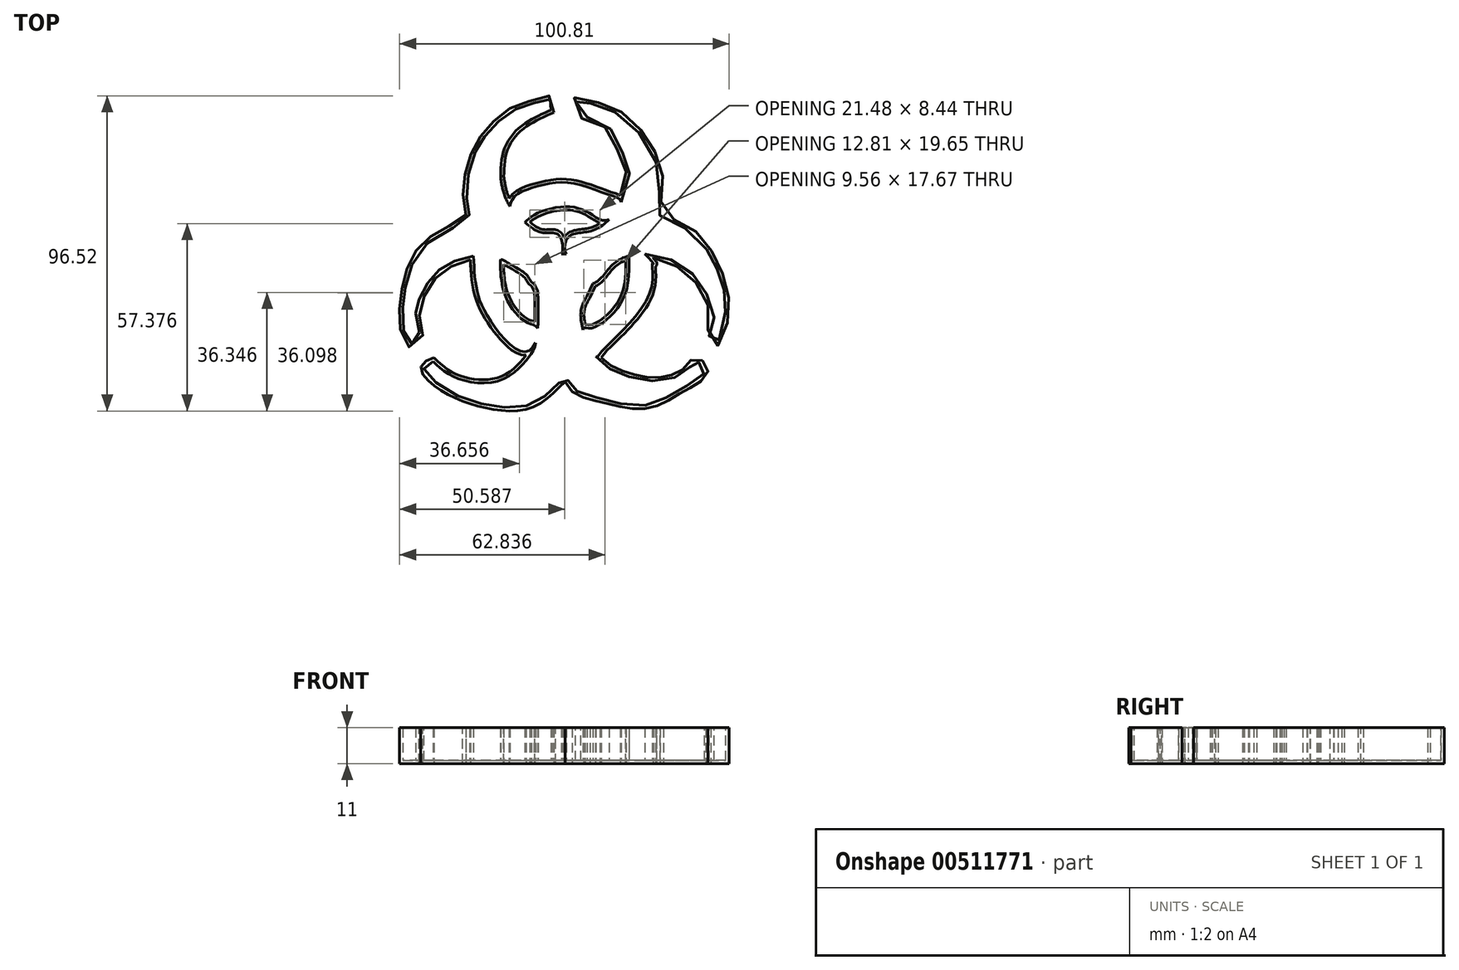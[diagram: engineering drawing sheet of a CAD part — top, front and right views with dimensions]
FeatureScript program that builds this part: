
annotation { "Feature Type Name" : "Feature", "Feature Type Description" : "" }
export const myFeature = defineFeature(function(context is Context, id is Id, definition is map)
    precondition{}
    {
        {
            var Q0;
            Q0=qCreatedBy(makeId("Top.planeOp"),FACE);
            var sketch = newSketch(context, id + "F0", { "sketchPlane" : qUnion([Q0])});
            skFitSpline(sketch, "E0", {"points": [v(-7.67, 51.18) * mm, v(-12.75, 48.8) * mm, v(-18.4, 44.85) * mm, v(-22.23, 38.53) * mm, v(-23.14, 30.74) * mm], "startDerivative": vector(-22.22, -9.67) * mm, "endDerivative": vector(-0.85, -30.02) * mm});
            skFitSpline(sketch, "E1", {"points": [v(-23.14, 30.74) * mm, v(-21.9, 24.98) * mm, v(-18.62, 19.45) * mm, v(-14.33, 15.72) * mm, v(-10.04, 13.57) * mm, v(-5.3, 12.9) * mm, v(-4.5, 7.14) * mm, v(-6.23, 6.65) * mm, v(-8.7, 3.81) * mm, v(-8.56, 0.6) * mm, v(-12.94, -1.87) * mm, v(-14.76, 0.22) * mm, v(-18.58, 3.02) * mm, v(-23.14, 5.54) * mm, v(-26.6, 6.37) * mm, v(-31.42, 6.5) * mm, v(-39.15, 4.06) * mm, v(-44.05, 0.16) * mm, v(-48.07, -6.62) * mm, v(-49.07, -10.95) * mm, v(-48.13, -18.6) * mm, v(-51.11, -20.32) * mm, v(-53.05, -11.45) * mm, v(-52.02, -1.94) * mm, v(-45.68, 10.35) * mm, v(-32.93, 18.54) * mm, v(-33.61, 24.7) * mm, v(-31.21, 37.43) * mm, v(-27.68, 43.51) * mm, v(-20.34, 50.45) * mm, v(-12.75, 53.38) * mm, v(-7.67, 54.36) * mm, v(-7.67, 51.18) * mm], "startDerivative": vector(27.16, -188.43) * mm, "endDerivative": vector(-39.63, -181.1) * mm});
            skFitSpline(sketch, "E2", {"points": [v(-20.34, 21.78) * mm, v(-18.62, 24.98) * mm, v(-11.51, 27.94) * mm, v(-1.52, 28.86) * mm, v(10.79, 24.98) * mm, v(13.71, 23.02) * mm, v(9.56, 17.48) * mm, v(4.33, 19.45) * mm, v(-2.75, 21.63) * mm, v(-12.13, 19.45) * mm, v(-15.77, 16.82) * mm], "startDerivative": vector(14.78, 47.04) * mm, "endDerivative": vector(-37.06, -33.58) * mm});
            skFitSpline(sketch, "E3", {"points": [v(0.64, 50.45) * mm, v(8.64, 47.32) * mm, v(13.71, 38.86) * mm, v(16.17, 33.4) * mm, v(13.71, 23.02) * mm, v(5.25, 14.4) * mm, v(-2.44, 12.25) * mm, v(-3.05, 7.17) * mm, v(-0.77, 6) * mm, v(1.57, 2.33) * mm, v(0.96, 0.2) * mm, v(5.13, -1.84) * mm, v(11.34, 4.06) * mm, v(21, 7.14) * mm, v(30.07, 4.87) * mm, v(36.99, -0.42) * mm, v(40.96, -7.54) * mm, v(41.97, -14.46) * mm, v(40.65, -18.53) * mm, v(42.69, -20.16) * mm, v(45.47, -12.22) * mm, v(45.47, -5.3) * mm, v(43.6, 1.31) * mm, v(41.36, 6.2) * mm, v(34.04, 14.64) * mm, v(25.18, 19.45) * mm, v(25.62, 27.91) * mm, v(21.83, 40.46) * mm, v(12.1, 50.45) * mm, v(4.03, 53.38) * mm, v(0.23, 54.36) * mm, v(0.64, 50.45) * mm]});
            skFitSpline(sketch, "E4", {"points": [v(21, 7.14) * mm, v(23.7, 4.14) * mm, v(23.39, 4.3) * mm, v(22.6, -4.59) * mm, v(7.62, -23) * mm, v(5.98, -24.22) * mm, v(2.1, -15.64) * mm, v(3.94, -15.64) * mm, v(13.71, -7.88) * mm, v(16.17, 6.57) * mm], "startDerivative": vector(49.86, -54.06) * mm, "endDerivative": vector(-1.43, 92.76) * mm});
            skFitSpline(sketch, "E5", {"points": [v(5.13, -1.84) * mm, v(3.4, -5.68) * mm], "startDerivative": vector(-1.74, -3.84) * mm, "endDerivative": vector(-1.74, -3.84) * mm});
            skFitSpline(sketch, "E6", {"points": [v(0.96, 0.2) * mm, v(-0.95, -1.84) * mm], "startDerivative": vector(-1.92, -2.04) * mm, "endDerivative": vector(-1.92, -2.04) * mm});
            skFitSpline(sketch, "E7", {"points": [v(-8.56, 0.6) * mm, v(-6.68, -1.84) * mm], "startDerivative": vector(1.88, -2.44) * mm, "endDerivative": vector(1.88, -2.44) * mm});
            skFitSpline(sketch, "E8", {"points": [v(-12.94, -1.87) * mm, v(-11.23, -5.29) * mm], "startDerivative": vector(1.71, -3.41) * mm, "endDerivative": vector(1.71, -3.41) * mm});
            skFitSpline(sketch, "E9", {"points": [v(-5.3, 12.9) * mm, v(-2.44, 12.25) * mm], "startDerivative": vector(2.86, -0.65) * mm, "endDerivative": vector(2.86, -0.65) * mm});
            skFitSpline(sketch, "E10", {"points": [v(-4.5, 7.14) * mm, v(-3.05, 7.17) * mm], "startDerivative": vector(1.45, 0.04) * mm, "endDerivative": vector(1.45, 0.04) * mm});
            skFitSpline(sketch, "E11", {"points": [v(-23.14, 5.54) * mm, v(-23.14, 1.94) * mm, v(-21.35, -6.55) * mm, v(-15.1, -13.79) * mm, v(-11.61, -16.04) * mm, v(-15.1, -22.78) * mm, v(-26.6, -12.8) * mm, v(-30.58, -3.06) * mm, v(-31.42, 6.5) * mm], "startDerivative": vector(-1.25, -38.8) * mm, "endDerivative": vector(-3.41, 73.3) * mm});
            skFitSpline(sketch, "E12", {"points": [v(-43.81, -25.77) * mm, v(-36.82, -30.76) * mm, v(-23.14, -31.51) * mm, v(-14.76, -24.77) * mm, v(-12.37, -20.1) * mm, v(-11.61, -9.8) * mm, v(-11.8, -4.15) * mm], "startDerivative": vector(35.95, -33.84) * mm, "endDerivative": vector(-2, 37.23) * mm});
            skFitSpline(sketch, "E13", {"points": [v(-43.81, -25.77) * mm, v(-46.56, -27.77) * mm, v(-40.07, -34.26) * mm, v(-26.6, -39.23) * mm, v(-14.76, -39.23) * mm, v(-6.68, -33.76) * mm, v(-3.12, -31.01) * mm, v(-1.13, -33.76) * mm, v(6.86, -37) * mm, v(21.09, -39.23) * mm, v(32.07, -34.26) * mm, v(39.31, -28.52) * mm, v(36.57, -25.77) * mm, v(34.07, -28.27) * mm, v(24.83, -31.76) * mm, v(12.85, -29.27) * mm, v(5.98, -24.22) * mm, v(1.37, -11.54) * mm, v(3.4, -5.68) * mm], "startDerivative": vector(-112.54, -43.6) * mm, "endDerivative": vector(63.22, 104.4) * mm});
            skSolve(sketch);
        }
        {
            var Q0;
            Q0 = qSketchRegion(id + "F0", true);
            extrude(context, id + "F1", {"entities" : qUnion([Q0]), "depth" : 10 * mm});
        }
        {
            var Q0;
            Q0=makeQuery(id+"F1.opExtrude","CAP_FACE",FACE,{"disambiguationData":[OSD([sQuery(id+"F0.wireOp",EDGE,"E0"),sQuery(id+"F0.wireOp",EDGE,"E1"),sQuery(id+"F0.wireOp",EDGE,"E2"),sQuery(id+"F0.wireOp",EDGE,"E3"),sQuery(id+"F0.wireOp",EDGE,"E4"),sQuery(id+"F0.wireOp",EDGE,"E5"),sQuery(id+"F0.wireOp",EDGE,"E8"),sQuery(id+"F0.wireOp",EDGE,"E10"),sQuery(id+"F0.wireOp",EDGE,"E11"),sQuery(id+"F0.wireOp",EDGE,"E12"),sQuery(id+"F0.wireOp",EDGE,"E13")])],"isStart":false});
            shell(context, id + "F2", {"entities" : qUnion([Q0]), "thickness" : 1 * mm, "oppositeDirection" : true});
        }
    });
